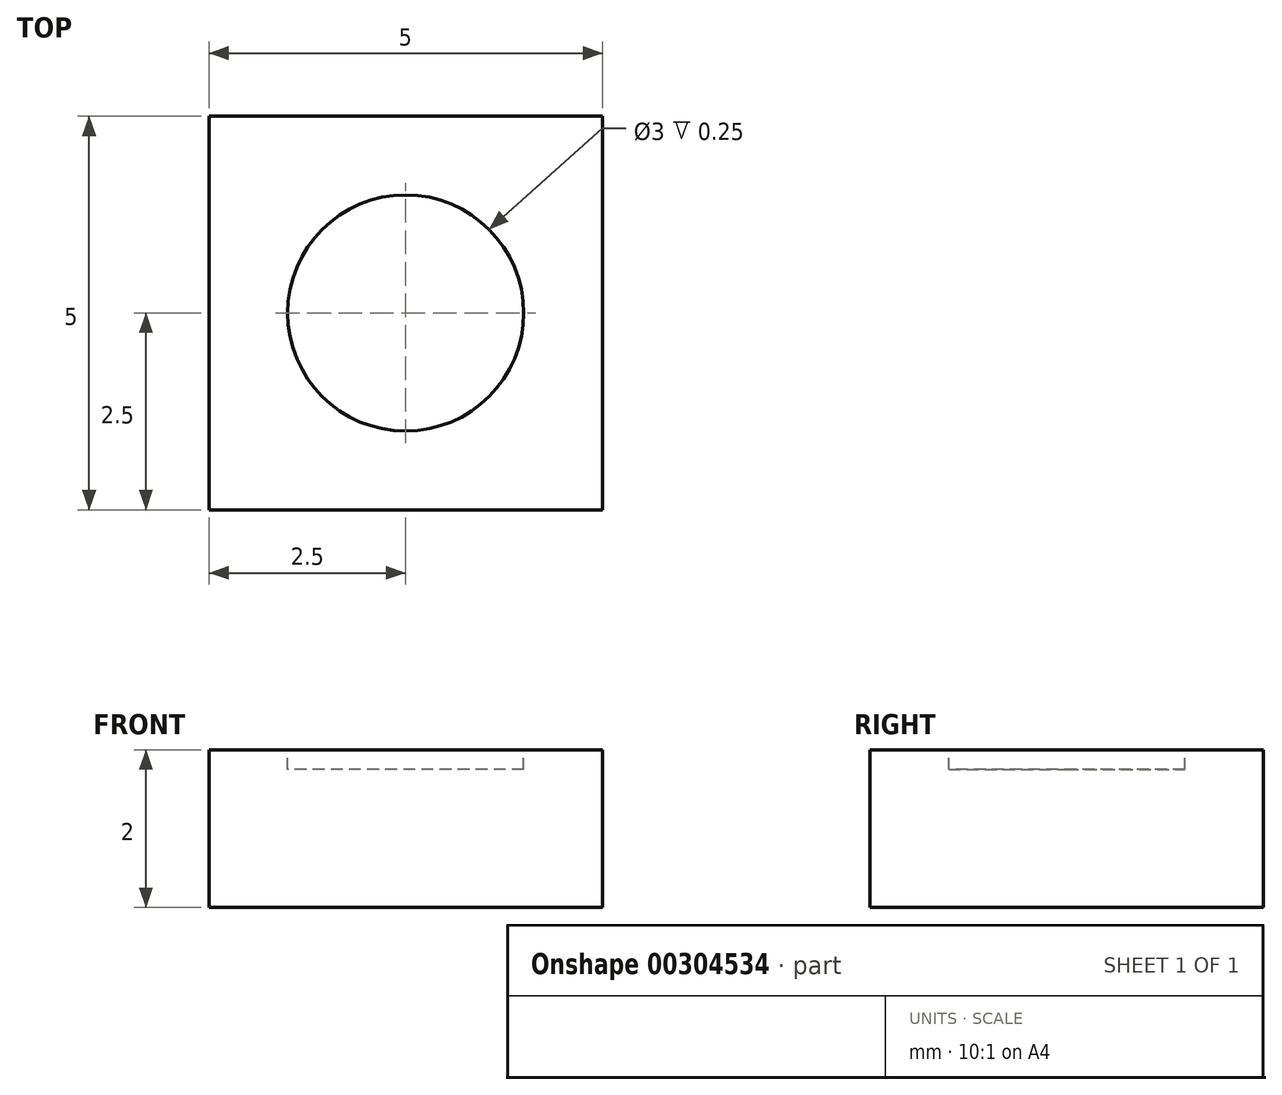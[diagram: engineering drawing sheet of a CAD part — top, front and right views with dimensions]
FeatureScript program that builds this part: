
annotation { "Feature Type Name" : "Feature", "Feature Type Description" : "" }
export const myFeature = defineFeature(function(context is Context, id is Id, definition is map)
    precondition{}
    {
        {
            var Q0;
            Q0=qCreatedBy(makeId("Top.planeOp"),FACE);
            var sketch = newSketch(context, id + "F0", { "sketchPlane" : qUnion([Q0])});
            skLineSegment(sketch, "E0.bottom", {"start": v(2.5, 2.5) * mm, "end": v(-2.5, 2.5) * mm});
            skLineSegment(sketch, "E0.top", {"start": v(2.5, -2.5) * mm, "end": v(-2.5, -2.5) * mm});
            skLineSegment(sketch, "E0.left", {"start": v(2.5, 2.5) * mm, "end": v(2.5, -2.5) * mm});
            skLineSegment(sketch, "E0.right", {"start": v(-2.5, 2.5) * mm, "end": v(-2.5, -2.5) * mm});
            skPoint(sketch, "E0.middle", {"position": v(0, 0) * mm});
            skSolve(sketch);
        }
        {
            var Q0;
            Q0 = qSketchRegion(id + "F0", true);
            extrude(context, id + "F1", {"entities" : qUnion([Q0]), "depth" : 2 * mm});
        }
        {
            var Q0;
            Q0=makeQuery(id+"F1.opExtrude","CAP_FACE",FACE,{"disambiguationData":[OSD([sQuery(id+"F0.wireOp",EDGE,"E0.bottom"),sQuery(id+"F0.wireOp",EDGE,"E0.top"),sQuery(id+"F0.wireOp",EDGE,"E0.left"),sQuery(id+"F0.wireOp",EDGE,"E0.right")])],"isStart":false});
            var sketch = newSketch(context, id + "F2", { "sketchPlane" : qUnion([Q0])});
            skCircle(sketch, "E1", {"center": v(0, 0) * mm, "radius": 1.5 * mm});
            skSolve(sketch);
        }
        {
            var Q0;
            Q0 = qSketchRegion(id + "F2", true);
            extrude(context, id + "F3", {"entities" : qUnion([Q0]), "operationType" : NewBodyOperationType.REMOVE, "oppositeDirection" : true, "depth" : .25 * mm});
        }
    });
